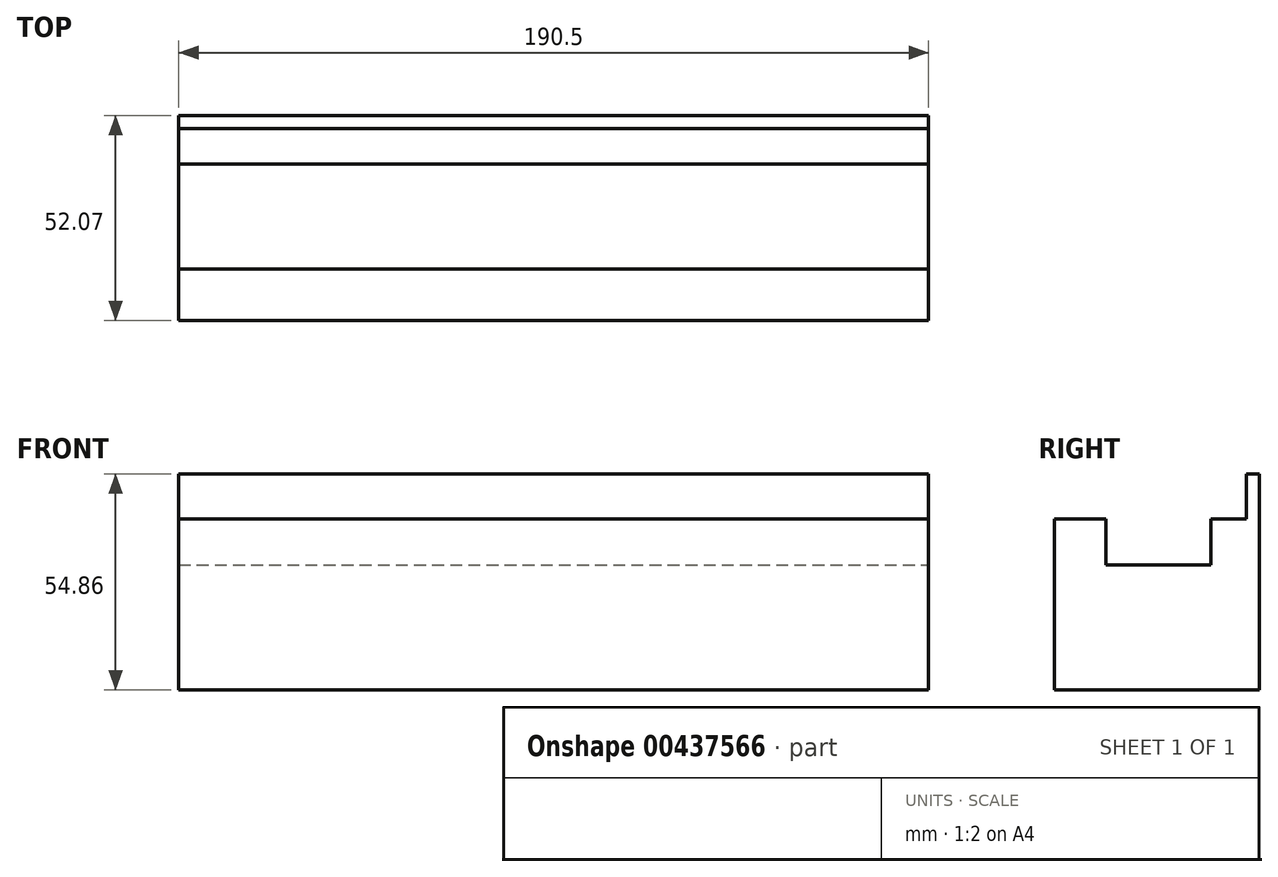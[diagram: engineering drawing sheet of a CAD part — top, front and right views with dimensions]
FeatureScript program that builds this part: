
annotation { "Feature Type Name" : "Feature", "Feature Type Description" : "" }
export const myFeature = defineFeature(function(context is Context, id is Id, definition is map)
    precondition{}
    {
        {
            var Q0;
            Q0=qCreatedBy(makeId("Top.planeOp"),FACE);
            var sketch = newSketch(context, id + "F0", { "sketchPlane" : qUnion([Q0])});
            skLineSegment(sketch, "E0.bottom", {"start": v(95.25, -10.87) * mm, "end": v(-95.25, -10.87) * mm});
            skLineSegment(sketch, "E0.top", {"start": v(95.25, 10.87) * mm, "end": v(-95.25, 10.87) * mm});
            skLineSegment(sketch, "E0.left", {"start": v(95.25, -10.87) * mm, "end": v(95.25, 10.87) * mm});
            skLineSegment(sketch, "E0.right", {"start": v(-95.25, -10.87) * mm, "end": v(-95.25, 10.87) * mm});
            skPoint(sketch, "E0.middle", {"position": v(0, 0) * mm});
            skSolve(sketch);
        }
        {
            var Q0;
            Q0=makeQuery(id+"F0.imprint","IMPRINT",FACE,{"disambiguationData":[TD([[makeQuery(id+"F0.imprint","IMPRINT",EDGE,{"derivedFrom":sQuery(id+"F0.wireOp",EDGE,"E0.bottom")}),-1.0]])]});
            extrude(context, id + "F1", {"entities" : qUnion([Q0]), "depth" : 54.86 * mm});
        }
        {
            var Q0;
            Q0=makeQuery(id+"F1.opExtrude","CAP_FACE",FACE,{"disambiguationData":[OSD([sQuery(id+"F0.wireOp",EDGE,"E0.bottom"),sQuery(id+"F0.wireOp",EDGE,"E0.top"),sQuery(id+"F0.wireOp",EDGE,"E0.left"),sQuery(id+"F0.wireOp",EDGE,"E0.right")])],"isStart":false});
            var sketch = newSketch(context, id + "F2", { "sketchPlane" : qUnion([Q0])});
            skPoint(sketch, "E1.0", {"position": v(-95.25, 10.87) * mm});
            skLineSegment(sketch, "E2.bottom", {"start": v(-95.25, 10.87) * mm, "end": v(95.25, 10.87) * mm});
            skLineSegment(sketch, "E2.top", {"start": v(-95.25, 7.57) * mm, "end": v(95.25, 7.57) * mm});
            skLineSegment(sketch, "E2.left", {"start": v(-95.25, 10.87) * mm, "end": v(-95.25, 7.57) * mm});
            skLineSegment(sketch, "E2.right", {"start": v(95.25, 10.87) * mm, "end": v(95.25, 7.57) * mm});
            skSolve(sketch);
        }
        {
            var Q0;
            {var subQ0=sQuery(id+"F2.wireOp",EDGE,"E2.top");Q0=makeQuery(id+"F2.imprint","IMPRINT",FACE,{"disambiguationData":[TD([[makeQuery(id+"F2.imprint","IMPRINT",EDGE,{"derivedFrom":subQ0}),-1.0]])]});}
            var sketch = newSketch(context, id + "F3", { "sketchPlane" : qUnion([Q0])});
            skPoint(sketch, "E3.0", {"position": v(-95.25, 7.57) * mm});
            skLineSegment(sketch, "E4.bottom", {"start": v(-95.25, 7.57) * mm, "end": v(95.25, 7.57) * mm});
            skLineSegment(sketch, "E4.top", {"start": v(-95.25, -10.97) * mm, "end": v(95.25, -10.97) * mm});
            skLineSegment(sketch, "E4.left", {"start": v(-95.25, 7.57) * mm, "end": v(-95.25, -10.97) * mm});
            skLineSegment(sketch, "E4.right", {"start": v(95.25, 7.57) * mm, "end": v(95.25, -10.97) * mm});
            skSolve(sketch);
        }
        {
            var Q0;
            Q0 = qSketchRegion(id + "F3", true);
            extrude(context, id + "F4", {"entities" : qUnion([Q0]), "operationType" : NewBodyOperationType.REMOVE, "oppositeDirection" : true, "depth" : 11.43 * mm});
        }
        {
            var Q0;
            {var subQ0=sQuery(id+"F2.wireOp",EDGE,"E2.top");Q0=makeQuery(id+"F2.imprint","IMPRINT",FACE,{"disambiguationData":[TD([[makeQuery(id+"F2.imprint","IMPRINT",EDGE,{"derivedFrom":subQ0}),-1.0]])]});}
            var sketch = newSketch(context, id + "F5", { "sketchPlane" : qUnion([Q0])});
            skPoint(sketch, "E5.0", {"position": v(-95.25, 7.57) * mm});
            skLineSegment(sketch, "E6.bottom", {"start": v(-95.25, 7.57) * mm, "end": v(95.25, 7.57) * mm});
            skLineSegment(sketch, "E6.top", {"start": v(-95.25, -1.42) * mm, "end": v(95.25, -1.42) * mm});
            skLineSegment(sketch, "E6.left", {"start": v(-95.25, 7.57) * mm, "end": v(-95.25, -1.42) * mm});
            skLineSegment(sketch, "E6.right", {"start": v(95.25, 7.57) * mm, "end": v(95.25, -1.42) * mm});
            skSolve(sketch);
        }
        {
            var Q0;
            Q0=qCreatedBy(makeId("Top.planeOp"),FACE);
            var sketch = newSketch(context, id + "F6", { "sketchPlane" : qUnion([Q0])});
            skPoint(sketch, "E7.0", {"position": v(95.25, 10.87) * mm});
            skLineSegment(sketch, "E8.bottom", {"start": v(95.25, 10.87) * mm, "end": v(-95.25, 10.87) * mm});
            skLineSegment(sketch, "E8.top", {"start": v(95.25, -41.2) * mm, "end": v(-95.25, -41.2) * mm});
            skLineSegment(sketch, "E8.left", {"start": v(95.25, 10.87) * mm, "end": v(95.25, -41.2) * mm});
            skLineSegment(sketch, "E8.right", {"start": v(-95.25, 10.87) * mm, "end": v(-95.25, -41.2) * mm});
            skSolve(sketch);
        }
        {
            var Q0;
            Q0 = qSketchRegion(id + "F6", true);
            extrude(context, id + "F7", {"entities" : qUnion([Q0]), "operationType" : NewBodyOperationType.ADD, "depth" : 43.43 * mm});
        }
        {
            var Q0;
            {var subQ0=sQuery(id+"F2.wireOp",EDGE,"E2.top");Q0=makeQuery(id+"F2.imprint","IMPRINT",FACE,{"disambiguationData":[TD([[makeQuery(id+"F2.imprint","IMPRINT",EDGE,{"derivedFrom":subQ0}),-1.0]])]});}
            var sketch = newSketch(context, id + "F8", { "sketchPlane" : qUnion([Q0])});
            skPoint(sketch, "E9.0", {"position": v(-95.25, -1.42) * mm});
            skLineSegment(sketch, "E10.bottom", {"start": v(-95.25, -1.42) * mm, "end": v(95.25, -1.42) * mm});
            skLineSegment(sketch, "E10.top", {"start": v(-95.25, -28.1) * mm, "end": v(95.25, -28.1) * mm});
            skLineSegment(sketch, "E10.left", {"start": v(-95.25, -1.42) * mm, "end": v(-95.25, -28.1) * mm});
            skLineSegment(sketch, "E10.right", {"start": v(95.25, -1.42) * mm, "end": v(95.25, -28.1) * mm});
            skSolve(sketch);
        }
        {
            var Q0;
            Q0 = qSketchRegion(id + "F8", true);
            extrude(context, id + "F9", {"entities" : qUnion([Q0]), "operationType" : NewBodyOperationType.REMOVE, "oppositeDirection" : true, "depth" : 23.1 * mm});
        }
    });
